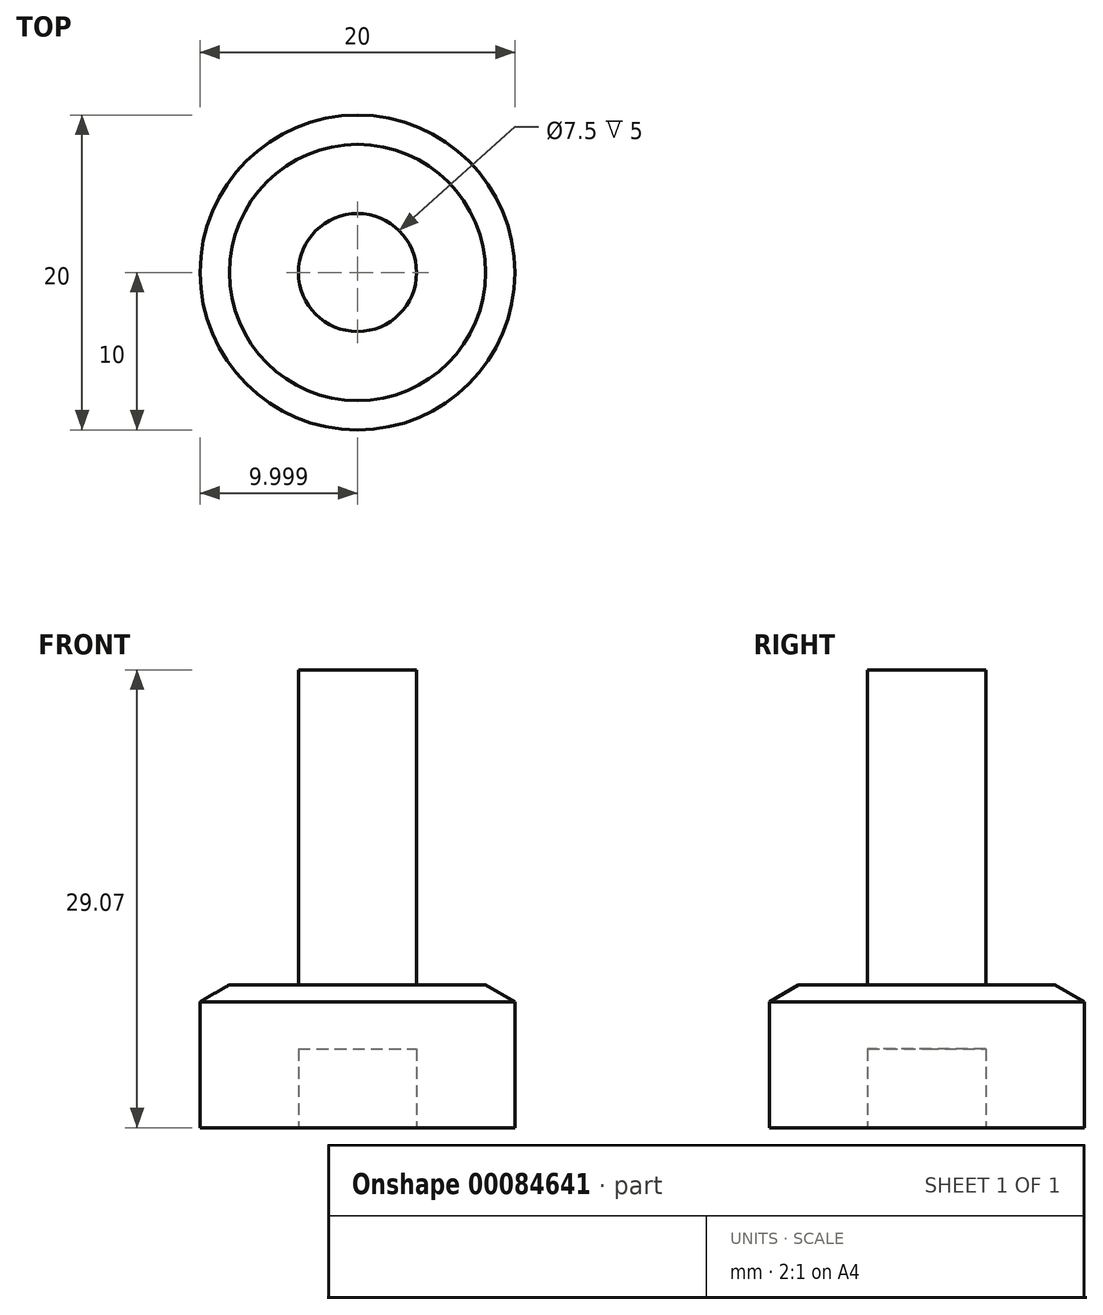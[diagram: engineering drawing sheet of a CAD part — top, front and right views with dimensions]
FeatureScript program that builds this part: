
annotation { "Feature Type Name" : "Feature", "Feature Type Description" : "" }
export const myFeature = defineFeature(function(context is Context, id is Id, definition is map)
    precondition{}
    {
        {
            var Q0;
            Q0=qCreatedBy(makeId("Front.planeOp"),FACE);
            var sketch = newSketch(context, id + "F0", { "sketchPlane" : qUnion([Q0])});
            skLineSegment(sketch, "E0.bottom", {"start": v(-30.55, 8) * mm, "end": v(-20.55, 8) * mm});
            skLineSegment(sketch, "E0.top", {"start": v(-30.55, 0) * mm, "end": v(-24.3, 0) * mm});
            skLineSegment(sketch, "E0.left", {"start": v(-30.55, 8) * mm, "end": v(-30.55, 0) * mm});
            skPoint(sketch, "E1", {"position": v(-20.55, 8) * mm});
            skPoint(sketch, "E2", {"position": v(-20.55, 0) * mm});
            skPoint(sketch, "E3", {"position": v(-20.55, 9.07) * mm});
            skLineSegment(sketch, "E4", {"start": v(-20.55, 8) * mm, "end": v(-20.55, 9.07) * mm});
            skLineSegment(sketch, "E5", {"start": v(-30.55, 8) * mm, "end": v(-28.7, 9.07) * mm});
            skLineSegment(sketch, "E6", {"start": v(-28.7, 9.07) * mm, "end": v(-20.55, 9.07) * mm});
            skLineSegment(sketch, "E7", {"start": v(-20.55, 8) * mm, "end": v(-20.55, 5) * mm});
            skPoint(sketch, "E0.right.end.orphan", {"position": v(-10.55, 0) * mm});
            skPoint(sketch, "E8.start.orphan", {"position": v(-10.55, 8) * mm});
            skLineSegment(sketch, "E9", {"start": v(-20.55, 9.07) * mm, "end": v(-20.55, 29.07) * mm});
            skLineSegment(sketch, "E10", {"start": v(-20.55, 29.07) * mm, "end": v(-24.3, 29.07) * mm});
            skLineSegment(sketch, "E11", {"start": v(-24.3, 29.07) * mm, "end": v(-24.3, 0) * mm});
            skPoint(sketch, "E12.start.orphan", {"position": v(-20.55, 4) * mm});
            skLineSegment(sketch, "E13", {"start": v(-20.55, 5) * mm, "end": v(-24.3, 5) * mm});
            skPoint(sketch, "E14", {"position": v(-20.55, 5) * mm});
            skSolve(sketch);
        }
        {
            var Q0;
            {var subQ0=sQuery(id+"F0.wireOp",EDGE,"E9");Q0=makeQuery(id+"F0.imprint","IMPRINT",FACE,{"disambiguationData":[TD([[makeQuery(id+"F0.imprint","IMPRINT",EDGE,{"derivedFrom":subQ0}),1.0]])]});}
            var Q1;
            {var subQ5=sQuery(id+"F0.wireOp",EDGE,"E0.top");Q1=makeQuery(id+"F0.imprint","IMPRINT",FACE,{"disambiguationData":[TD([[makeQuery(id+"F0.imprint","IMPRINT",EDGE,{"derivedFrom":subQ5}),1.0]])]});}
            var Q2;
            {var subQ0=sQuery(id+"F0.wireOp",EDGE,"E5");Q2=makeQuery(id+"F0.imprint","IMPRINT",FACE,{"disambiguationData":[TD([[makeQuery(id+"F0.imprint","IMPRINT",EDGE,{"derivedFrom":subQ0}),-1.0]])]});}
            var Q3;
            {var subQ0=sQuery(id+"F0.wireOp",EDGE,"E7");Q3=makeQuery(id+"F0.imprint","IMPRINT",FACE,{"disambiguationData":[TD([[makeQuery(id+"F0.imprint","IMPRINT",EDGE,{"derivedFrom":subQ0}),-1.0]])]});}
            var Q4;
            {var subQ0=sQuery(id+"F0.wireOp",EDGE,"E4");Q4=makeQuery(id+"F0.imprint","IMPRINT",FACE,{"disambiguationData":[TD([[makeQuery(id+"F0.imprint","IMPRINT",EDGE,{"derivedFrom":subQ0}),1.0]])]});}
            var Q5;
            Q5=sQuery(id+"F0.wireOp",EDGE,"E9");
            revolve(context, id + "F1", {"entities" : qUnion([Q0, Q1, Q2, Q3, Q4]), "axis" : qUnion([Q5]), "revolveType" : RevolveType.FULL});
        }
    });
